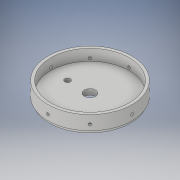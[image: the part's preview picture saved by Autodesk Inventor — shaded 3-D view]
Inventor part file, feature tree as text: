
AUTODESK INVENTOR PART (.ipt)
format: ipt  version: 2017 SP1 (Build 210196100, 196)  size: 167,424 bytes
history: native  units: in
note: dims shown in document units (in); Inventor stores cm internally (conversion verified against a paired STEP export)
features: sketch x5, extrude x4, plane x1, hole x1, pattern_circular x1
ambient origin geometry x8: Origin, YZ Plane, XZ Plane, XY Plane, X Axis, Y Axis, Z Axis, Center Point
bodies: Solid1 (feature_tree)
feature tree (12):
  extrude  "Extrusion1"  Depth=0.25in TaperAngle=0.0deg
  extrude  "Extrusion2"  Depth=0.25in TaperAngle=0.0deg
  extrude  "Extrusion3"  Depth=7.0in
  plane  "Work Plane1"
  hole  "Hole1"  [1 undecoded]
  pattern_circular  "Circular Pattern1"  Count=8 Angle=360.0deg
  extrude  "Extrusion4"  Depth=0.5in
  sketch  "Sketch1"  dims[d0=7.25in d1=0.25in d2=0.0in]
  sketch  "Sketch2"  dims[d3=7.5in d4=0.25in d5=0.0in]
  sketch  "Sketch3"  dims[d6=7.5in d7=7.0in]
  sketch  "Sketch4"  dims[d8=1.0in d9=0.0in d10=0.5in]
  sketch  "Sketch5"  dims[d11=0.25in d12=0.75in d13=0.375in d14=0.25in d15=0.5635in d16=1.0in d17=0.8108in d18=3.1496in d19=360.0deg d21=0.5in d22=1.0in d23=2.0in d24=0.5in d25=0.0in]
note: 1 required parameter value undecoded (feature->parameter linkage not recoverable at this tier; creation-order binding heuristic only, values carry confidence <= 0.55)
